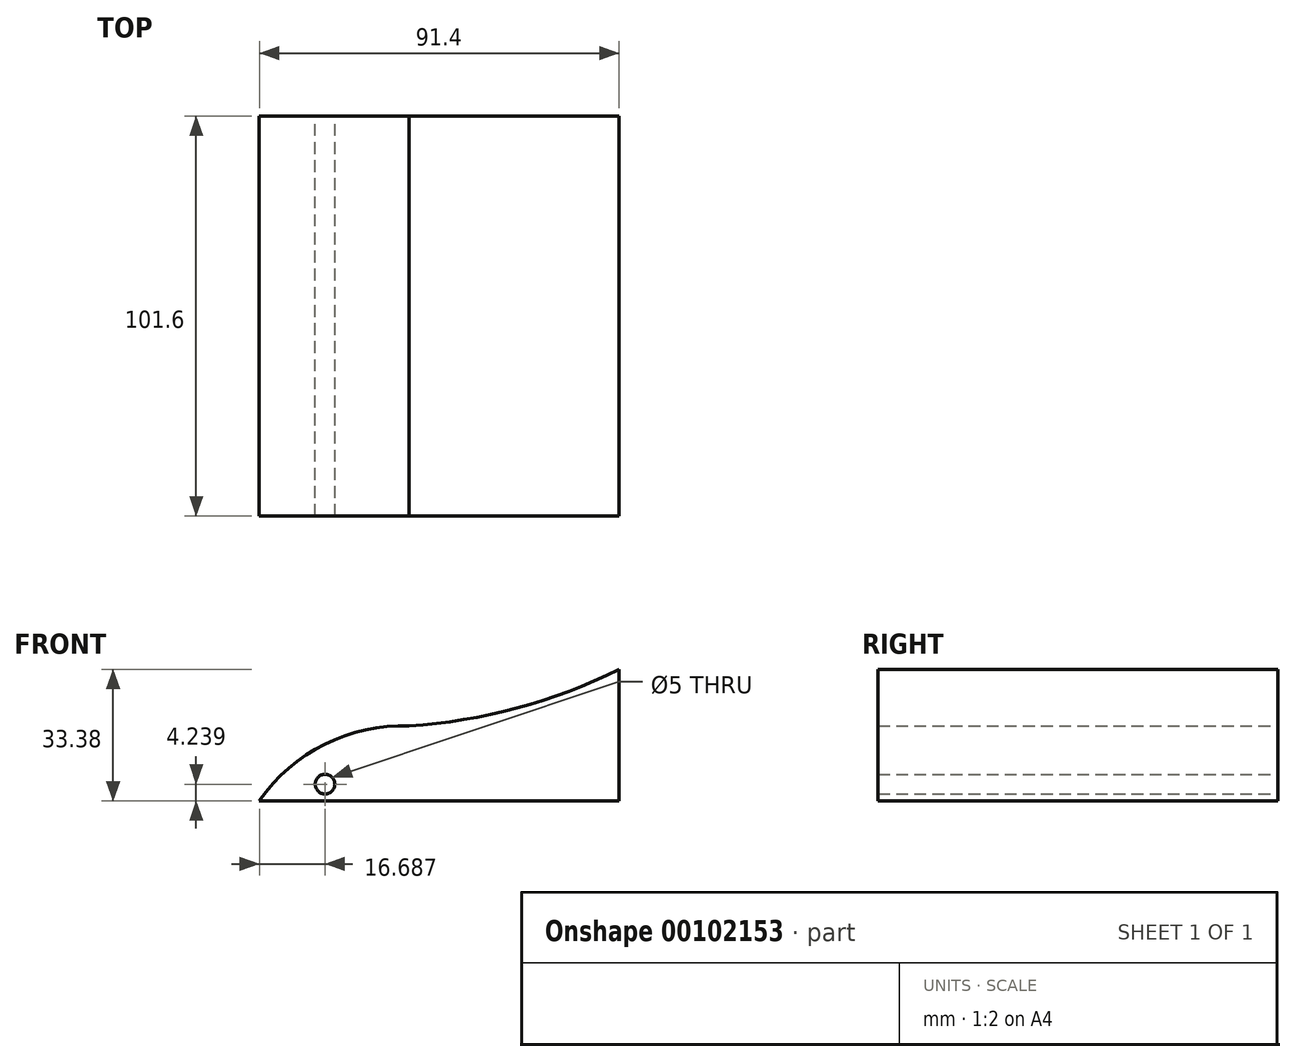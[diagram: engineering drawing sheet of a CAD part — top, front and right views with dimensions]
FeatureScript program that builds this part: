
annotation { "Feature Type Name" : "Feature", "Feature Type Description" : "" }
export const myFeature = defineFeature(function(context is Context, id is Id, definition is map)
    precondition{}
    {
        {
            var Q0;
            Q0=qCreatedBy(makeId("Front.planeOp"),FACE);
            var sketch = newSketch(context, id + "F0", { "sketchPlane" : qUnion([Q0])});
            skLineSegment(sketch, "E0", {"start": v(-62.52, 0) * mm, "end": v(-24.42, 0) * mm});
            skArc(sketch, "E1", {"start": v(-24.42, 19.05) * mm, "mid": v(-45.9, 14.38) * mm, "end": v(-62.52, 0) * mm});
            skArc(sketch, "E2", {"start": v(-24.42, 19.05) * mm, "mid": v(2.94, 23.56) * mm, "end": v(28.88, 33.38) * mm});
            skLineSegment(sketch, "E3", {"start": v(28.88, 33.38) * mm, "end": v(28.88, 0) * mm});
            skLineSegment(sketch, "E4", {"start": v(28.88, 0) * mm, "end": v(-24.42, 0) * mm});
            skCircle(sketch, "E5", {"center": v(-45.83, 4.24) * mm, "radius": 2.5 * mm});
            skSolve(sketch);
        }
        {
            var Q0;
            Q0 = qSketchRegion(id + "F0", true);
            extrude(context, id + "F1", {"entities" : qUnion([Q0]), "depth" : 101.6 * mm});
        }
    });
